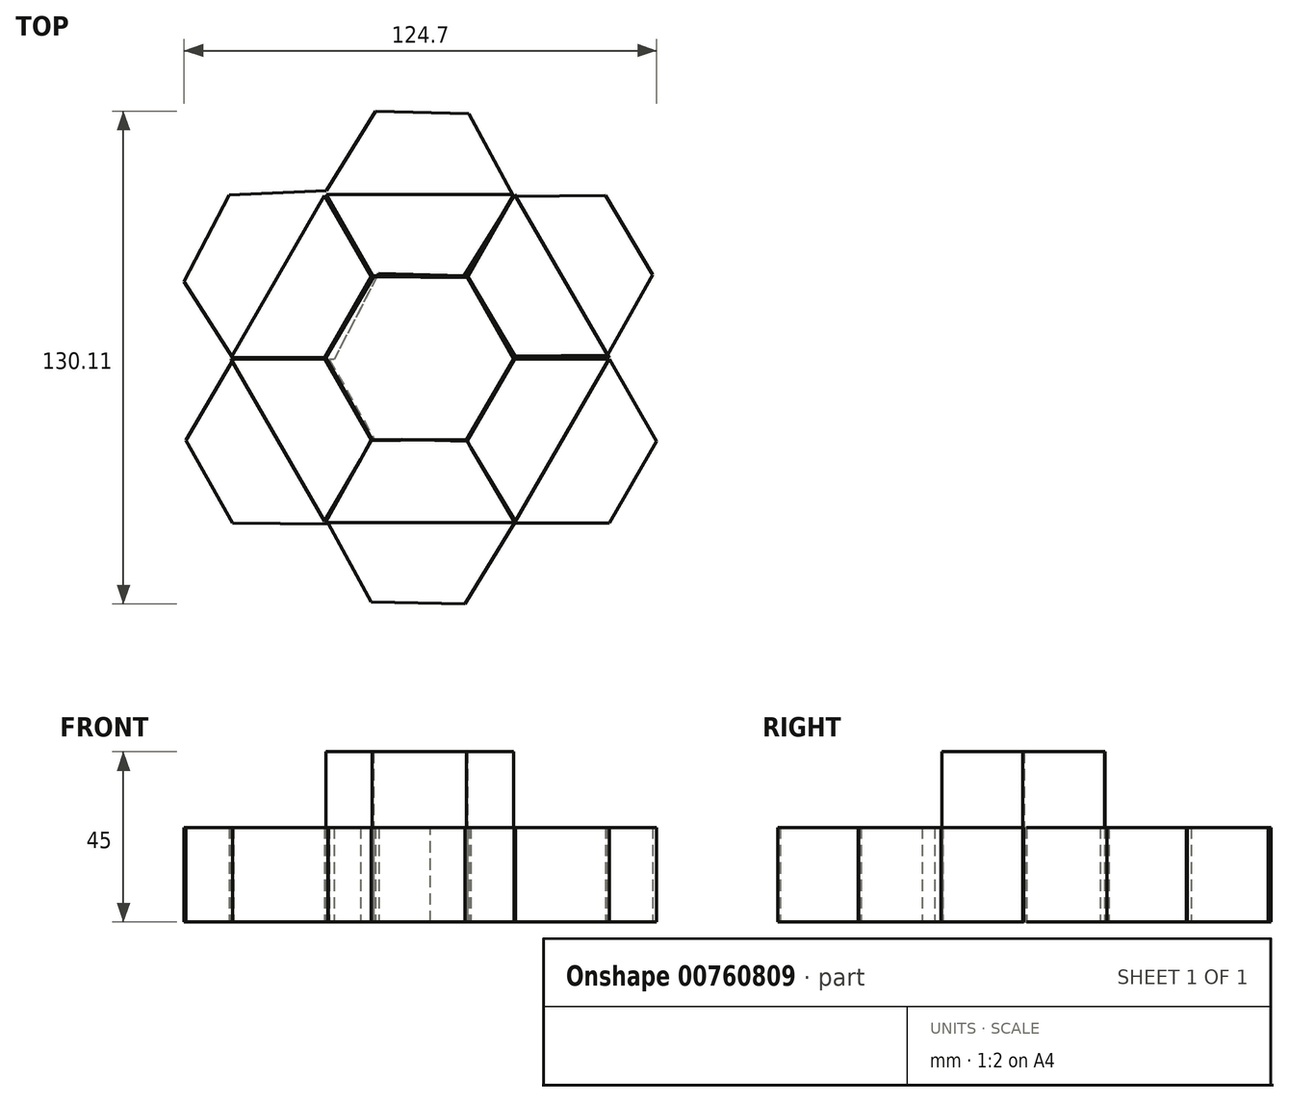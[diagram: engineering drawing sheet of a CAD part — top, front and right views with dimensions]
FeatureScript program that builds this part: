
annotation { "Feature Type Name" : "Feature", "Feature Type Description" : "" }
export const myFeature = defineFeature(function(context is Context, id is Id, definition is map)
    precondition{}
    {
        {
            var Q0;
            Q0=qCreatedBy(makeId("Top.planeOp"),FACE);
            var sketch = newSketch(context, id + "F0", { "sketchPlane" : qUnion([Q0])});
            skCircle(sketch, "E0.cCircle", {"center": v(0, 0) * mm, "radius": 50 * mm, "construction": true});
            skLineSegment(sketch, "E0.0", {"start": v(50, 0) * mm, "end": v(25, -43.3) * mm});
            skLineSegment(sketch, "E0.1", {"start": v(25, -43.3) * mm, "end": v(-25, -43.3) * mm});
            skLineSegment(sketch, "E0.2", {"start": v(-25, -43.3) * mm, "end": v(-50, 0) * mm});
            skLineSegment(sketch, "E0.3", {"start": v(-50, 0) * mm, "end": v(-25, 43.3) * mm});
            skLineSegment(sketch, "E0.4", {"start": v(-25, 43.3) * mm, "end": v(25, 43.3) * mm});
            skLineSegment(sketch, "E0.5", {"start": v(25, 43.3) * mm, "end": v(50, 0) * mm});
            skCircle(sketch, "E1.cCircle", {"center": v(-37.5, 21.65) * mm, "radius": 24.68 * mm, "construction": true});
            skPoint(sketch, "E1.cCircle.perimeterSnap0", {"position": v(-37.5, 21.65) * mm});
            skLineSegment(sketch, "E1.0", {"start": v(-62.18, 21.65) * mm, "end": v(-49.84, 43.02) * mm});
            skPoint(sketch, "E1.0.startSnap0", {"position": v(-37.5, 21.65) * mm});
            skLineSegment(sketch, "E1.1", {"start": v(-49.84, 43.02) * mm, "end": v(-25.16, 43.02) * mm});
            skLineSegment(sketch, "E1.2", {"start": v(-25.16, 43.02) * mm, "end": v(-12.82, 21.65) * mm});
            skLineSegment(sketch, "E1.3", {"start": v(-12.82, 21.65) * mm, "end": v(-25.16, 0.28) * mm});
            skLineSegment(sketch, "E1.4", {"start": v(-25.16, 0.28) * mm, "end": v(-49.84, 0.28) * mm});
            skLineSegment(sketch, "E1.5", {"start": v(-49.84, 0.28) * mm, "end": v(-62.18, 21.65) * mm});
            skCircle(sketch, "E2.cCircle", {"center": v(-37.5, -21.65) * mm, "radius": 24.7 * mm, "construction": true});
            skLineSegment(sketch, "E2.0", {"start": v(-49.91, -43.02) * mm, "end": v(-62.2, -21.58) * mm});
            skLineSegment(sketch, "E2.1", {"start": v(-62.2, -21.58) * mm, "end": v(-49.8, -0.22) * mm});
            skLineSegment(sketch, "E2.2", {"start": v(-49.8, -0.22) * mm, "end": v(-25.09, -0.29) * mm});
            skLineSegment(sketch, "E2.3", {"start": v(-25.09, -0.29) * mm, "end": v(-12.8, -21.72) * mm});
            skLineSegment(sketch, "E2.4", {"start": v(-12.8, -21.72) * mm, "end": v(-25.2, -43.08) * mm});
            skLineSegment(sketch, "E2.5", {"start": v(-25.2, -43.08) * mm, "end": v(-49.91, -43.02) * mm});
            skCircle(sketch, "E3.cCircle", {"center": v(0, -43.3) * mm, "radius": 25.14 * mm, "construction": true});
            skLineSegment(sketch, "E3.0", {"start": v(12.93, -64.86) * mm, "end": v(-12.2, -65.28) * mm});
            skLineSegment(sketch, "E3.1", {"start": v(-12.2, -65.28) * mm, "end": v(-25.14, -43.72) * mm});
            skLineSegment(sketch, "E3.2", {"start": v(-25.14, -43.72) * mm, "end": v(-12.93, -21.74) * mm});
            skLineSegment(sketch, "E3.3", {"start": v(-12.93, -21.74) * mm, "end": v(12.2, -21.32) * mm});
            skLineSegment(sketch, "E3.4", {"start": v(12.2, -21.32) * mm, "end": v(25.14, -42.88) * mm});
            skLineSegment(sketch, "E3.5", {"start": v(25.14, -42.88) * mm, "end": v(12.93, -64.86) * mm});
            skPoint(sketch, "E4.cCircle.perimeterSnap0", {"position": v(37.5, 21.65) * mm});
            skPoint(sketch, "E4.0.startSnap0", {"position": v(37.5, 21.65) * mm});
            skLineSegment(sketch, "E5.4", {"start": v(-12.53, 21.39) * mm, "end": v(-25.25, 43.2) * mm});
            skCircle(sketch, "E6.cCircle", {"center": v(37.5, -21.65) * mm, "radius": 25.06 * mm, "construction": true});
            skPoint(sketch, "E6.cCircle.perimeterSnap0", {"position": v(37.5, -21.65) * mm});
            skLineSegment(sketch, "E6.0", {"start": v(62.56, -21.65) * mm, "end": v(50.03, -43.35) * mm});
            skPoint(sketch, "E6.0.startSnap0", {"position": v(37.5, -21.65) * mm});
            skLineSegment(sketch, "E6.1", {"start": v(50.03, -43.35) * mm, "end": v(24.97, -43.35) * mm});
            skLineSegment(sketch, "E6.2", {"start": v(24.97, -43.35) * mm, "end": v(12.44, -21.65) * mm});
            skLineSegment(sketch, "E6.3", {"start": v(12.44, -21.65) * mm, "end": v(24.97, 0.05) * mm});
            skLineSegment(sketch, "E6.4", {"start": v(24.97, 0.05) * mm, "end": v(50.03, 0.05) * mm});
            skLineSegment(sketch, "E6.5", {"start": v(50.03, 0.05) * mm, "end": v(62.56, -21.65) * mm});
            skCircle(sketch, "E7.cCircle", {"center": v(37.5, 21.65) * mm, "radius": 25.06 * mm, "construction": true});
            skLineSegment(sketch, "E7.0", {"start": v(62.56, 21.65) * mm, "end": v(50.03, -0.05) * mm});
            skLineSegment(sketch, "E7.1", {"start": v(50.03, -0.05) * mm, "end": v(24.97, -0.05) * mm});
            skLineSegment(sketch, "E7.2", {"start": v(24.97, -0.05) * mm, "end": v(12.44, 21.65) * mm});
            skLineSegment(sketch, "E7.3", {"start": v(12.44, 21.65) * mm, "end": v(24.97, 43.35) * mm});
            skLineSegment(sketch, "E7.4", {"start": v(24.97, 43.35) * mm, "end": v(50.03, 43.35) * mm});
            skLineSegment(sketch, "E7.5", {"start": v(50.03, 43.35) * mm, "end": v(62.56, 21.65) * mm});
            skCircle(sketch, "E8.cCircle", {"center": v(0, 43.3) * mm, "radius": 24.72 * mm, "construction": true});
            skLineSegment(sketch, "E8.0", {"start": v(12.44, 64.67) * mm, "end": v(24.72, 43.21) * mm});
            skLineSegment(sketch, "E8.1", {"start": v(24.72, 43.21) * mm, "end": v(12.28, 21.84) * mm});
            skLineSegment(sketch, "E8.2", {"start": v(12.28, 21.84) * mm, "end": v(-12.44, 21.94) * mm});
            skLineSegment(sketch, "E8.3", {"start": v(-12.44, 21.94) * mm, "end": v(-24.72, 43.4) * mm});
            skLineSegment(sketch, "E8.4", {"start": v(-24.72, 43.4) * mm, "end": v(-12.28, 64.76) * mm});
            skLineSegment(sketch, "E8.5", {"start": v(-12.28, 64.76) * mm, "end": v(12.44, 64.67) * mm});
            skSolve(sketch);
        }
        {
            var Q0;
            {var subQ1=sQuery(id+"F0.wireOp",EDGE,"E0.1");var subQ5=sQuery(id+"F0.wireOp",EDGE,"E3.5");var subQ6=makeQuery(id+"F0.imprint","INTERSECT",VERTEX,{"derivedFrom":[subQ1,subQ5]});Q0=makeQuery(id+"F0.imprint","IMPRINT",FACE,{"disambiguationData":[TD([[makeQuery(id+"F0.imprint","IMPRINT",EDGE,{"disambiguationData":[TD([[subQ6,-1.0]])],"derivedFrom":subQ1}),-1.0]])]});}
            var Q1;
            {var subQ6=sQuery(id+"F0.wireOp",EDGE,"E2.2");Q1=makeQuery(id+"F0.imprint","IMPRINT",FACE,{"disambiguationData":[TD([[makeQuery(id+"F0.imprint","IMPRINT",EDGE,{"derivedFrom":subQ6}),-1.0]])]});}
            var Q2;
            {var subQ0=sQuery(id+"F0.wireOp",EDGE,"E1.2");Q2=makeQuery(id+"F0.imprint","IMPRINT",FACE,{"disambiguationData":[TD([[makeQuery(id+"F0.imprint","IMPRINT",EDGE,{"derivedFrom":subQ0}),-1.0]])]});}
            var Q3;
            {var subQ1=sQuery(id+"F0.wireOp",EDGE,"E8.1");Q3=makeQuery(id+"F0.imprint","IMPRINT",FACE,{"disambiguationData":[TD([[makeQuery(id+"F0.imprint","IMPRINT",EDGE,{"derivedFrom":subQ1}),-1.0]])]});}
            var Q4;
            {var subQ3=sQuery(id+"F0.wireOp",EDGE,"E0.5");var subQ9=sQuery(id+"F0.wireOp",EDGE,"E0.4");var subQ11=makeQuery(id+"F0.imprint","INTERSECT",VERTEX,{"derivedFrom":[subQ9,subQ3]});Q4=makeQuery(id+"F0.imprint","IMPRINT",FACE,{"disambiguationData":[TD([[makeQuery(id+"F0.imprint","IMPRINT",EDGE,{"disambiguationData":[TD([[subQ11,1.0]])],"derivedFrom":subQ9}),-1.0]])]});}
            var Q5;
            {var subQ6=sQuery(id+"F0.wireOp",EDGE,"E0.1");var subQ7=sQuery(id+"F0.wireOp",EDGE,"E0.0");var subQ8=makeQuery(id+"F0.imprint","INTERSECT",VERTEX,{"derivedFrom":[subQ7,subQ6]});Q5=makeQuery(id+"F0.imprint","IMPRINT",FACE,{"disambiguationData":[TD([[makeQuery(id+"F0.imprint","IMPRINT",EDGE,{"disambiguationData":[TD([[subQ8,1.0]])],"derivedFrom":subQ7}),-1.0]])]});}
            extrude(context, id + "F1", {"entities" : qUnion([Q0, Q1, Q2, Q3, Q4, Q5]), "depth" : 25 * mm, "offsetDistance" : 25 * mm});
        }
        {
            var Q0;
            Q0=qCreatedBy(makeId("Top.planeOp"),FACE);
            var sketch = newSketch(context, id + "F2", { "sketchPlane" : qUnion([Q0])});
            skCircle(sketch, "E9.cCircle", {"center": v(0, 0) * mm, "radius": 24.78 * mm, "construction": true});
            skLineSegment(sketch, "E9.0", {"start": v(12.55, 21.36) * mm, "end": v(24.78, -0.19) * mm});
            skLineSegment(sketch, "E9.1", {"start": v(24.78, -0.19) * mm, "end": v(12.23, -21.55) * mm});
            skLineSegment(sketch, "E9.2", {"start": v(12.23, -21.55) * mm, "end": v(-12.55, -21.36) * mm});
            skLineSegment(sketch, "E9.3", {"start": v(-12.55, -21.36) * mm, "end": v(-24.78, 0.19) * mm});
            skLineSegment(sketch, "E9.4", {"start": v(-24.78, 0.19) * mm, "end": v(-12.23, 21.55) * mm});
            skLineSegment(sketch, "E9.5", {"start": v(-12.23, 21.55) * mm, "end": v(12.55, 21.36) * mm});
            skSolve(sketch);
        }
        {
            var Q0;
            Q0 = qSketchRegion(id + "F2", true);
            extrude(context, id + "F3", {"entities" : qUnion([Q0]), "operationType" : NewBodyOperationType.ADD, "depth" : 45 * mm, "offsetDistance" : 25 * mm});
        }
        {
            var Q0;
            Q0=qCreatedBy(makeId("Top.planeOp"),FACE);
            var sketch = newSketch(context, id + "F4", { "sketchPlane" : qUnion([Q0])});
            skCircle(sketch, "E10.cCircle", {"center": v(0, 43.57) * mm, "radius": 24.68 * mm, "construction": true});
            skLineSegment(sketch, "E10.0", {"start": v(-11.7, 65.3) * mm, "end": v(12.98, 64.56) * mm});
            skLineSegment(sketch, "E10.1", {"start": v(12.98, 64.56) * mm, "end": v(24.67, 42.83) * mm});
            skLineSegment(sketch, "E10.2", {"start": v(24.67, 42.83) * mm, "end": v(11.7, 21.83) * mm});
            skLineSegment(sketch, "E10.3", {"start": v(11.7, 21.83) * mm, "end": v(-12.98, 22.57) * mm});
            skLineSegment(sketch, "E10.4", {"start": v(-12.98, 22.57) * mm, "end": v(-24.67, 44.31) * mm});
            skLineSegment(sketch, "E10.5", {"start": v(-24.67, 44.31) * mm, "end": v(-11.7, 65.3) * mm});
            skCircle(sketch, "E11.cCircle", {"center": v(0, -43.03) * mm, "radius": 24.82 * mm, "construction": true});
            skLineSegment(sketch, "E11.0", {"start": v(12.9, -21.83) * mm, "end": v(24.81, -43.6) * mm});
            skLineSegment(sketch, "E11.1", {"start": v(24.81, -43.6) * mm, "end": v(11.9, -64.8) * mm});
            skLineSegment(sketch, "E11.2", {"start": v(11.9, -64.8) * mm, "end": v(-12.9, -64.23) * mm});
            skLineSegment(sketch, "E11.3", {"start": v(-12.9, -64.23) * mm, "end": v(-24.81, -42.46) * mm});
            skLineSegment(sketch, "E11.4", {"start": v(-24.81, -42.46) * mm, "end": v(-11.9, -21.26) * mm});
            skLineSegment(sketch, "E11.5", {"start": v(-11.9, -21.26) * mm, "end": v(12.9, -21.83) * mm});
            skCircle(sketch, "E12.cCircle", {"center": v(-36.67, -21.83) * mm, "radius": 25.1 * mm, "construction": true});
            skLineSegment(sketch, "E12.0", {"start": v(-49.06, 0) * mm, "end": v(-23.96, -0.18) * mm});
            skLineSegment(sketch, "E12.1", {"start": v(-23.96, -0.18) * mm, "end": v(-11.57, -22.01) * mm});
            skLineSegment(sketch, "E12.2", {"start": v(-11.57, -22.01) * mm, "end": v(-24.28, -43.66) * mm});
            skLineSegment(sketch, "E12.3", {"start": v(-24.28, -43.66) * mm, "end": v(-49.38, -43.48) * mm});
            skLineSegment(sketch, "E12.4", {"start": v(-49.38, -43.48) * mm, "end": v(-61.77, -21.65) * mm});
            skLineSegment(sketch, "E12.5", {"start": v(-61.77, -21.65) * mm, "end": v(-49.06, 0) * mm});
            skCircle(sketch, "E13.cCircle", {"center": v(37.47, -21.83) * mm, "radius": 25 * mm, "construction": true});
            skLineSegment(sketch, "E13.0", {"start": v(62.47, -21.83) * mm, "end": v(49.97, -43.48) * mm});
            skLineSegment(sketch, "E13.1", {"start": v(49.97, -43.48) * mm, "end": v(24.97, -43.48) * mm});
            skLineSegment(sketch, "E13.2", {"start": v(24.97, -43.48) * mm, "end": v(12.47, -21.83) * mm});
            skLineSegment(sketch, "E13.3", {"start": v(12.47, -21.83) * mm, "end": v(24.97, -0.18) * mm});
            skLineSegment(sketch, "E13.4", {"start": v(24.97, -0.18) * mm, "end": v(49.97, -0.18) * mm});
            skLineSegment(sketch, "E13.5", {"start": v(49.97, -0.18) * mm, "end": v(62.47, -21.83) * mm});
            skCircle(sketch, "E14.cCircle", {"center": v(-36.51, 21.45) * mm, "radius": 25.74 * mm, "construction": true});
            skPoint(sketch, "E14.cCircle.centerSnap0", {"position": v(-36.51, -0.1) * mm});
            skLineSegment(sketch, "E14.0", {"start": v(-24.67, 44.31) * mm, "end": v(-10.8, 22.63) * mm});
            skLineSegment(sketch, "E14.1", {"start": v(-10.8, 22.63) * mm, "end": v(-22.63, -0.23) * mm});
            skLineSegment(sketch, "E14.2", {"start": v(-22.63, -0.23) * mm, "end": v(-48.35, -1.4) * mm});
            skLineSegment(sketch, "E14.3", {"start": v(-48.35, -1.4) * mm, "end": v(-62.23, 20.28) * mm});
            skLineSegment(sketch, "E14.4", {"start": v(-62.23, 20.28) * mm, "end": v(-50.39, 43.14) * mm});
            skLineSegment(sketch, "E14.5", {"start": v(-50.39, 43.14) * mm, "end": v(-24.67, 44.31) * mm});
            skCircle(sketch, "E15.cCircle", {"center": v(37.05, 21.83) * mm, "radius": 24.37 * mm, "construction": true});
            skLineSegment(sketch, "E15.0", {"start": v(24.67, 42.83) * mm, "end": v(49.04, 43.05) * mm});
            skLineSegment(sketch, "E15.1", {"start": v(49.04, 43.05) * mm, "end": v(61.42, 22.06) * mm});
            skLineSegment(sketch, "E15.2", {"start": v(61.42, 22.06) * mm, "end": v(49.43, 0.84) * mm});
            skLineSegment(sketch, "E15.3", {"start": v(49.43, 0.84) * mm, "end": v(25.06, 0.61) * mm});
            skLineSegment(sketch, "E15.4", {"start": v(25.06, 0.61) * mm, "end": v(12.68, 21.6) * mm});
            skLineSegment(sketch, "E15.5", {"start": v(12.68, 21.6) * mm, "end": v(24.67, 42.83) * mm});
            skLineSegment(sketch, "E16", {"start": v(-24.81, -42.46) * mm, "end": v(25.19, -43.6) * mm});
            skLineSegment(sketch, "E17", {"start": v(25.19, -43.6) * mm, "end": v(49.97, -0.18) * mm});
            skSolve(sketch);
        }
        {
            var Q0;
            Q0 = qSketchRegion(id + "F4", true);
            extrude(context, id + "F5", {"entities" : qUnion([Q0]), "depth" : 25 * mm, "offsetDistance" : 25 * mm});
        }
    });
